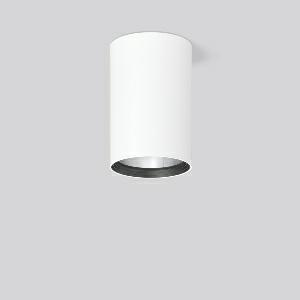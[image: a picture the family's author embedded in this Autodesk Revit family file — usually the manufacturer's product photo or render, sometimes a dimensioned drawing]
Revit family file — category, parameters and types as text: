
# Revit family: heledon_maxi_a_931224_002_2_76_3891
name_source: partatom
category: Lighting Fixtures
units: mm (PartAtom-declared; Revit-internal decimal feet)

## family parameters
Cut with Voids When Loaded = No
Host = Face
Light Source = No
Part Type = Normal
Room Calculation Point = No
Round Connector Dimension = Use Diameter
Shared = No

## types (1)
- HELEDON maxi A (1 x LED Modul 927, 4100 lm, 2700)
    Apparent Load = 35 VA
    Approval mark = CE
    CIE Flux Codes = 100 100 100 100 100
    Color Rendering = 92
    Color Temperature = 2700
    Default Elevation = 1800 mm
    Description = Series: HELEDON maxi
Cylindrical surface-mounted downlight. Housing: die-cast aluminium, powder-coated. Internal ceiling frame polycarbonate with bayonet mounting. Black plastic ring and recessed LED to prevent glare from the side. Optical assembly with reflector made of MIRO-Silver with 98% total light reflection for outstanding efficiency - can be changed without tools. Best colour rendering index Ra>90. Suitable for Ceiling mounting. Easy installation with a separate ceiling frame with bayonet mounting and plug connection. Driver integrated. Connected via plug-in connector. High quality converter without flickering and stroboscopic effect. The following accessories can be mounted without use of tools: interchangeable lenses, decorative glasses, honeycomb louvre, clear and frosted diffusers, white interchangeable plastic ring. 
Colour: traffic white, matt (RAL 9016)
Diameter: 123 mm
Height: 183 mm
Lamp: LED
Socket: without socket
Colour temperature: 2700K
Colour rendering index (CRI): 92
System power: 35 W
Rated luminous flux: 4100 lm
Luminous efficiency: 117 lm/W
Control gear: Converter, dimmable, DALI
Protection class: I
Type of protection: IP 20
    Height = 183 mm
    Lamp = 1 x LED Modul 927
    Lamp Light Flux = 4100 lm
    Lamp count = 1
    Length = 123 mm
    Lifetime = 50000 h
    Luminous efficacy = 117 lm/W
    Manufacturer = RZB
    ModVariant = No
    Model = 931224.002.2.76
    Mounting Place = Ceiling
    Mounting Type = Surface mounted
    Number of Poles = 1
    OnlyDefault = Yes
    Power Factor = 1
    Product Name = HELEDON maxi A
    Product group = Surface mounted downlights
    ProductGroupID = 302
    Protection Class = Protection class I
    Protection Degree = IP 20
    RLX_Detail_Level = 1
    RLX_Emergency_Light_Flux = 0 lm
    RLX_Emergency_Type = 0
    RLX_Emergency_Type_DB = No
    RlxData = <blob elided: 99625 chars, md5=25efbad7>
    Socket = socket
    Standby Power = 0 W
    System Light Flux = 4100 lm
    System Power = 35 W
    Type Comments = Product without accessories
    Type Image = 931192.002.jpg
    URL = http://relux.com
    VarID = ---
    Voltage = 230 V
    Voltage Range = 220-240 V
    Weight = 0.00 kg
    Width = 0 mm  [stored 0 ft]

note: [stored X ft] marks values corroborated as IEEE doubles in the binary element streams (Revit-internal decimal feet)

## geometry (parser evidence)
native form markers: Blend x4, Sweep x11
no freeform markers — native parametric forms only
